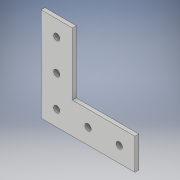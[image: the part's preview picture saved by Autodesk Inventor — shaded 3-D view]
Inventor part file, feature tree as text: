
AUTODESK INVENTOR PART (.ipt)
format: ipt  version: 2018 (Build 220112000, 112)  size: 111,616 bytes
history: native  units: in
note: dims shown in document units (in); Inventor stores cm internally (conversion verified against a paired STEP export)
features: extrude x1, sketch x1
ambient origin geometry x8: Origin, YZ Plane, XZ Plane, XY Plane, X Axis, Y Axis, Z Axis, Center Point
bodies: Solid1 (feature_tree)
feature tree (2):
  extrude  "Extrusion1"  Depth=1.0in
  sketch  "Sketch1"  dims[d0=3.0in d1=1.0in d2=1.0in d3=3.0in d4=0.5in d5=1.0in d6=1.0in d7=1.0in d8=1.0in d9=0.2031in d10=0.125in d11=0.0in]
